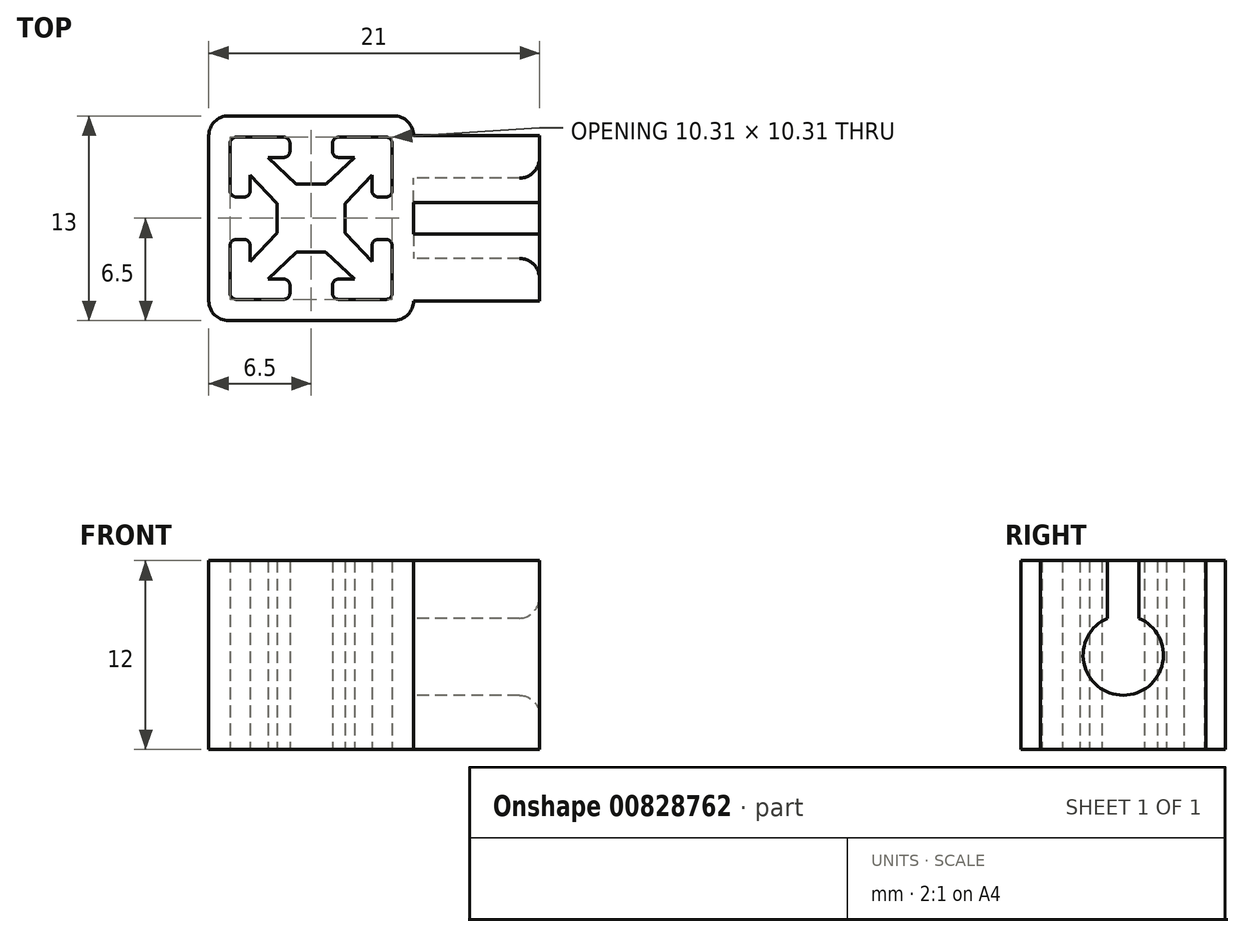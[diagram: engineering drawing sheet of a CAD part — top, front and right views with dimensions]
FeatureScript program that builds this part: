
annotation { "Feature Type Name" : "Feature", "Feature Type Description" : "" }
export const myFeature = defineFeature(function(context is Context, id is Id, definition is map)
    precondition{}
    {
        {
            var Q0;
            Q0=qCreatedBy(makeId("Top.planeOp"),FACE);
            var sketch = newSketch(context, id + "F0", { "sketchPlane" : qUnion([Q0])});
            skArc(sketch, "E0.0", {"start": v(6.5, 5.25) * mm, "mid": v(6.13, 6.13) * mm, "end": v(5.25, 6.5) * mm});
            skLineSegment(sketch, "E0.1", {"start": v(6.5, -5.25) * mm, "end": v(6.5, 5.25) * mm});
            skLineSegment(sketch, "E0.2", {"start": v(5.25, 6.5) * mm, "end": v(-5.25, 6.5) * mm});
            skArc(sketch, "E0.3", {"start": v(5.25, -6.5) * mm, "mid": v(6.13, -6.13) * mm, "end": v(6.5, -5.25) * mm});
            skArc(sketch, "E0.4", {"start": v(-5.25, 6.5) * mm, "mid": v(-6.13, 6.13) * mm, "end": v(-6.5, 5.25) * mm});
            skLineSegment(sketch, "E0.5", {"start": v(-6.5, 5.25) * mm, "end": v(-6.5, -5.25) * mm});
            skArc(sketch, "E0.6", {"start": v(-6.5, -5.25) * mm, "mid": v(-6.13, -6.13) * mm, "end": v(-5.25, -6.5) * mm});
            skLineSegment(sketch, "E0.7", {"start": v(-5.25, -6.5) * mm, "end": v(5.25, -6.5) * mm});
            skSolve(sketch);
        }
        {
            var Q0;
            Q0=qSketchRegion(id+"F0",true);
            extrude(context, id + "F1", {"entities" : qUnion([Q0]), "endBound" : BoundingType.SYMMETRIC, "oppositeDirection" : true, "depth" : 12 * mm, "offsetDistance" : 25 * mm});
        }
        {
            var Q0;
            Q0=qCreatedBy(makeId("Top.planeOp"),FACE);
            var sketch = newSketch(context, id + "F2", { "sketchPlane" : qUnion([Q0])});
            skLineSegment(sketch, "E1.0", {"start": v(0.96, -2.18) * mm, "end": v(2.75, -3.86) * mm});
            skArc(sketch, "E1.1", {"start": v(0.96, -2.18) * mm, "mid": v(0.93, -2.16) * mm, "end": v(0.89, -2.16) * mm});
            skLineSegment(sketch, "E1.2", {"start": v(0.89, -2.16) * mm, "end": v(-0.89, -2.16) * mm});
            skArc(sketch, "E1.3", {"start": v(-0.89, -2.16) * mm, "mid": v(-0.93, -2.16) * mm, "end": v(-0.96, -2.18) * mm});
            skLineSegment(sketch, "E1.4", {"start": v(-0.96, -2.18) * mm, "end": v(-2.75, -3.86) * mm});
            skLineSegment(sketch, "E1.5", {"start": v(-2.75, -3.86) * mm, "end": v(-1.75, -3.86) * mm});
            skArc(sketch, "E1.6", {"start": v(-1.35, -4.27) * mm, "mid": v(-1.47, -3.98) * mm, "end": v(-1.75, -3.86) * mm});
            skLineSegment(sketch, "E1.7", {"start": v(-1.35, -4.27) * mm, "end": v(-1.35, -4.75) * mm});
            skArc(sketch, "E1.8", {"start": v(-1.75, -5.15) * mm, "mid": v(-1.47, -5.04) * mm, "end": v(-1.35, -4.75) * mm});
            skLineSegment(sketch, "E1.9", {"start": v(-1.75, -5.15) * mm, "end": v(-4.75, -5.15) * mm});
            skArc(sketch, "E1.10", {"start": v(-5.15, -4.75) * mm, "mid": v(-5.04, -5.04) * mm, "end": v(-4.75, -5.15) * mm});
            skLineSegment(sketch, "E1.11", {"start": v(-5.15, -1.75) * mm, "end": v(-5.15, -4.75) * mm});
            skArc(sketch, "E1.12", {"start": v(-4.75, -1.35) * mm, "mid": v(-5.04, -1.47) * mm, "end": v(-5.15, -1.75) * mm});
            skLineSegment(sketch, "E1.13", {"start": v(-4.27, -1.35) * mm, "end": v(-4.75, -1.35) * mm});
            skArc(sketch, "E1.14", {"start": v(-3.86, -1.75) * mm, "mid": v(-3.98, -1.47) * mm, "end": v(-4.27, -1.35) * mm});
            skLineSegment(sketch, "E1.15", {"start": v(-3.86, -2.75) * mm, "end": v(-3.86, -1.75) * mm});
            skLineSegment(sketch, "E1.16", {"start": v(-2.18, -0.96) * mm, "end": v(-3.86, -2.75) * mm});
            skArc(sketch, "E1.17", {"start": v(-2.18, -0.96) * mm, "mid": v(-2.16, -0.93) * mm, "end": v(-2.16, -0.89) * mm});
            skArc(sketch, "E1.18", {"start": v(5.15, 4.75) * mm, "mid": v(5.04, 5.04) * mm, "end": v(4.75, 5.15) * mm});
            skLineSegment(sketch, "E1.19", {"start": v(5.15, 1.75) * mm, "end": v(5.15, 4.75) * mm});
            skArc(sketch, "E1.20", {"start": v(4.75, 1.35) * mm, "mid": v(5.04, 1.47) * mm, "end": v(5.15, 1.75) * mm});
            skLineSegment(sketch, "E1.21", {"start": v(4.27, 1.35) * mm, "end": v(4.75, 1.35) * mm});
            skArc(sketch, "E1.22", {"start": v(3.86, 1.75) * mm, "mid": v(3.98, 1.47) * mm, "end": v(4.27, 1.35) * mm});
            skLineSegment(sketch, "E1.23", {"start": v(3.86, 2.75) * mm, "end": v(3.86, 1.75) * mm});
            skLineSegment(sketch, "E1.24", {"start": v(2.18, 0.96) * mm, "end": v(3.86, 2.75) * mm});
            skArc(sketch, "E1.25", {"start": v(2.18, 0.96) * mm, "mid": v(2.16, 0.93) * mm, "end": v(2.16, 0.89) * mm});
            skLineSegment(sketch, "E1.26", {"start": v(2.16, 0.89) * mm, "end": v(2.16, -0.89) * mm});
            skArc(sketch, "E1.27", {"start": v(2.16, -0.89) * mm, "mid": v(2.16, -0.93) * mm, "end": v(2.18, -0.96) * mm});
            skLineSegment(sketch, "E1.28", {"start": v(2.18, -0.96) * mm, "end": v(3.86, -2.75) * mm});
            skLineSegment(sketch, "E1.29", {"start": v(3.86, -2.75) * mm, "end": v(3.86, -1.75) * mm});
            skArc(sketch, "E1.30", {"start": v(1.35, -4.75) * mm, "mid": v(1.47, -5.04) * mm, "end": v(1.75, -5.15) * mm});
            skLineSegment(sketch, "E1.31", {"start": v(1.35, -4.27) * mm, "end": v(1.35, -4.75) * mm});
            skArc(sketch, "E1.32", {"start": v(1.75, -3.86) * mm, "mid": v(1.47, -3.98) * mm, "end": v(1.35, -4.27) * mm});
            skLineSegment(sketch, "E1.33", {"start": v(2.75, -3.86) * mm, "end": v(1.75, -3.86) * mm});
            skLineSegment(sketch, "E1.34", {"start": v(1.75, -5.15) * mm, "end": v(4.75, -5.15) * mm});
            skArc(sketch, "E1.35", {"start": v(4.75, -5.15) * mm, "mid": v(5.04, -5.04) * mm, "end": v(5.15, -4.75) * mm});
            skLineSegment(sketch, "E1.36", {"start": v(5.15, -1.75) * mm, "end": v(5.15, -4.75) * mm});
            skArc(sketch, "E1.37", {"start": v(5.15, -1.75) * mm, "mid": v(5.04, -1.47) * mm, "end": v(4.75, -1.35) * mm});
            skLineSegment(sketch, "E1.38", {"start": v(4.27, -1.35) * mm, "end": v(4.75, -1.35) * mm});
            skArc(sketch, "E1.39", {"start": v(4.27, -1.35) * mm, "mid": v(3.98, -1.47) * mm, "end": v(3.86, -1.75) * mm});
            skLineSegment(sketch, "E1.40", {"start": v(1.75, 5.15) * mm, "end": v(4.75, 5.15) * mm});
            skArc(sketch, "E1.41", {"start": v(1.75, 5.15) * mm, "mid": v(1.47, 5.04) * mm, "end": v(1.35, 4.75) * mm});
            skLineSegment(sketch, "E1.42", {"start": v(1.35, 4.27) * mm, "end": v(1.35, 4.75) * mm});
            skArc(sketch, "E1.43", {"start": v(1.35, 4.27) * mm, "mid": v(1.47, 3.98) * mm, "end": v(1.75, 3.86) * mm});
            skLineSegment(sketch, "E1.44", {"start": v(2.75, 3.86) * mm, "end": v(1.75, 3.86) * mm});
            skLineSegment(sketch, "E1.45", {"start": v(0.96, 2.18) * mm, "end": v(2.75, 3.86) * mm});
            skArc(sketch, "E1.46", {"start": v(0.89, 2.16) * mm, "mid": v(0.93, 2.16) * mm, "end": v(0.96, 2.18) * mm});
            skLineSegment(sketch, "E1.47", {"start": v(-0.89, 2.16) * mm, "end": v(0.89, 2.16) * mm});
            skArc(sketch, "E1.48", {"start": v(-0.96, 2.18) * mm, "mid": v(-0.93, 2.16) * mm, "end": v(-0.89, 2.16) * mm});
            skLineSegment(sketch, "E1.49", {"start": v(-0.96, 2.18) * mm, "end": v(-2.75, 3.86) * mm});
            skLineSegment(sketch, "E1.50", {"start": v(-2.75, 3.86) * mm, "end": v(-1.75, 3.86) * mm});
            skArc(sketch, "E1.51", {"start": v(-1.75, 3.86) * mm, "mid": v(-1.47, 3.98) * mm, "end": v(-1.35, 4.27) * mm});
            skLineSegment(sketch, "E1.52", {"start": v(-1.35, 4.27) * mm, "end": v(-1.35, 4.75) * mm});
            skArc(sketch, "E1.53", {"start": v(-1.35, 4.75) * mm, "mid": v(-1.47, 5.04) * mm, "end": v(-1.75, 5.15) * mm});
            skLineSegment(sketch, "E1.54", {"start": v(-1.75, 5.15) * mm, "end": v(-4.75, 5.15) * mm});
            skArc(sketch, "E1.55", {"start": v(-4.75, 5.15) * mm, "mid": v(-5.04, 5.04) * mm, "end": v(-5.15, 4.75) * mm});
            skLineSegment(sketch, "E1.56", {"start": v(-5.15, 1.75) * mm, "end": v(-5.15, 4.75) * mm});
            skArc(sketch, "E1.57", {"start": v(-5.15, 1.75) * mm, "mid": v(-5.04, 1.47) * mm, "end": v(-4.75, 1.35) * mm});
            skLineSegment(sketch, "E1.58", {"start": v(-4.27, 1.35) * mm, "end": v(-4.75, 1.35) * mm});
            skArc(sketch, "E1.59", {"start": v(-4.27, 1.35) * mm, "mid": v(-3.98, 1.47) * mm, "end": v(-3.86, 1.75) * mm});
            skLineSegment(sketch, "E1.60", {"start": v(-3.86, 2.75) * mm, "end": v(-3.86, 1.75) * mm});
            skLineSegment(sketch, "E1.61", {"start": v(-2.18, 0.96) * mm, "end": v(-3.86, 2.75) * mm});
            skArc(sketch, "E1.62", {"start": v(-2.16, 0.89) * mm, "mid": v(-2.16, 0.93) * mm, "end": v(-2.18, 0.96) * mm});
            skLineSegment(sketch, "E1.63", {"start": v(-2.16, 0.89) * mm, "end": v(-2.16, -0.89) * mm});
            skSolve(sketch);
        }
        {
            var Q0;
            Q0=makeQuery(id+"F2.imprint","IMPRINT",FACE,{"disambiguationData":[TD([[makeQuery(id+"F2.imprint","IMPRINT",EDGE,{"derivedFrom":sQuery(id+"F2.wireOp",EDGE,"E1.0")}),1.0]])]});
            extrude(context, id + "F3", {"entities" : qUnion([Q0]), "operationType" : NewBodyOperationType.REMOVE, "endBound" : BoundingType.SYMMETRIC, "depth" : 20 * mm, "offsetDistance" : 25 * mm});
        }
        {
            var Q0;
            Q0=makeQuery(id+"F1.opExtrude","SWEPT_FACE",FACE,{"disambiguationData":[OSD([sQuery(id+"F0.wireOp",EDGE,"E0.1")])]});
            var sketch = newSketch(context, id + "F4", { "sketchPlane" : qUnion([Q0])});
            skArc(sketch, "E2", {"start": v(-1, 2.35) * mm, "mid": v(0, -2.55) * mm, "end": v(1, 2.35) * mm});
            skLineSegment(sketch, "E3", {"start": v(1, 6) * mm, "end": v(1, 2.35) * mm});
            skLineSegment(sketch, "E4", {"start": v(-1, 6) * mm, "end": v(-1, 2.35) * mm});
            skLineSegment(sketch, "E5", {"start": v(-1, 6) * mm, "end": v(1, 6) * mm});
            skSolve(sketch);
        }
        {
            var Q0;
            Q0=makeQuery(id+"F4.imprint","IMPRINT",FACE,{"disambiguationData":[TD([[makeQuery(id+"F4.imprint","IMPRINT",EDGE,{"derivedFrom":sQuery(id+"F4.wireOp",EDGE,"E2")}),-1.0]])]});
            extrude(context, id + "F5", {"entities" : qUnion([Q0]), "operationType" : NewBodyOperationType.ADD, "depth" : 8 * mm, "offsetDistance" : 25 * mm});
        }
        {
            var Q0;
            Q0=makeQuery(id+"F5.opExtrude","CAP_EDGE",EDGE,{"disambiguationData":[OSD([sQuery(id+"F4.wireOp",EDGE,"E2")])],"isStart":false});
            fillet(context, id + "F6", {"entities" : qUnion([Q0]), "radius" : 1.27 * mm, "tangentPropagation" : true, "allowEdgeOverflow" : false});
        }
    });
